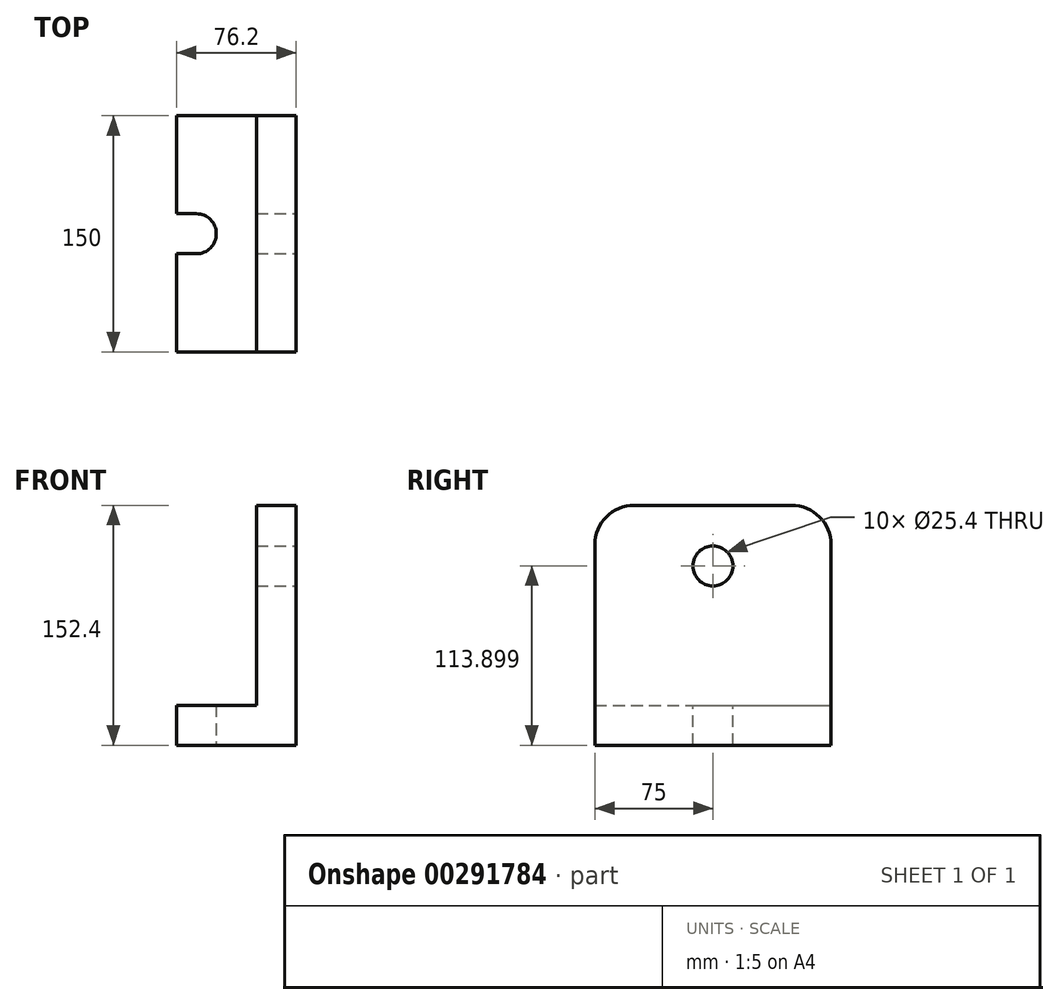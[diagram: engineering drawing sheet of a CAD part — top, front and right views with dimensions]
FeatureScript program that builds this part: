
annotation { "Feature Type Name" : "Feature", "Feature Type Description" : "" }
export const myFeature = defineFeature(function(context is Context, id is Id, definition is map)
    precondition{}
    {
        {
            var Q0;
            Q0=qCreatedBy(makeId("Front.planeOp"),FACE);
            var sketch = newSketch(context, id + "F0", { "sketchPlane" : qUnion([Q0])});
            skLineSegment(sketch, "E0.bottom", {"start": v(0, 0) * mm, "end": v(-76.2, 0) * mm});
            skLineSegment(sketch, "E0.top", {"start": v(-25.4, 25.4) * mm, "end": v(-76.2, 25.4) * mm});
            skLineSegment(sketch, "E0.right", {"start": v(-76.2, 0) * mm, "end": v(-76.2, 25.4) * mm});
            skLineSegment(sketch, "E1.top", {"start": v(0, 152.4) * mm, "end": v(-25.4, 152.4) * mm});
            skLineSegment(sketch, "E1.right", {"start": v(-25.4, 25.4) * mm, "end": v(-25.4, 152.4) * mm});
            skLineSegment(sketch, "E2", {"start": v(0, 152.4) * mm, "end": v(0, 0) * mm});
            skSolve(sketch);
        }
        {
            var Q0;
            Q0 = qSketchRegion(id + "F0", true);
            extrude(context, id + "F1", {"entities" : qUnion([Q0]), "endBound" : BoundingType.SYMMETRIC, "depth" : 150 * mm});
        }
        {
            var Q0;
            Q0=qCreatedBy(makeId("Right.planeOp"),FACE);
            var sketch = newSketch(context, id + "F2", { "sketchPlane" : qUnion([Q0])});
            skCircle(sketch, "E3", {"center": v(0, 113.9) * mm, "radius": 12.7 * mm});
            skSolve(sketch);
        }
        {
            var Q0;
            Q0=makeQuery(id+"F2.imprint","IMPRINT",FACE,{"disambiguationData":[TD([[makeQuery(id+"F2.imprint","IMPRINT",EDGE,{"derivedFrom":sQuery(id+"F2.wireOp",EDGE,"E3")}),1.0]])]});
            extrude(context, id + "F3", {"entities" : qUnion([Q0]), "operationType" : NewBodyOperationType.REMOVE, "oppositeDirection" : true, "depth" : 25.4 * mm});
        }
        {
            var Q0;
            Q0=qCreatedBy(makeId("Top.planeOp"),FACE);
            var sketch = newSketch(context, id + "F4", { "sketchPlane" : qUnion([Q0])});
            skLineSegment(sketch, "E4.bottom", {"start": v(-63.52, 12.7) * mm, "end": v(-76.22, 12.7) * mm});
            skLineSegment(sketch, "E4.top", {"start": v(-63.52, -12.7) * mm, "end": v(-76.22, -12.7) * mm});
            skLineSegment(sketch, "E4.right", {"start": v(-76.22, 12.7) * mm, "end": v(-76.22, -12.7) * mm});
            skPoint(sketch, "E4.middle", {"position": v(-69.87, 0) * mm});
            skArc(sketch, "E5", {"start": v(-63.52, -12.7) * mm, "mid": v(-50.82, 0) * mm, "end": v(-63.52, 12.7) * mm});
            skSolve(sketch);
        }
        {
            var Q0;
            Q0 = qSketchRegion(id + "F4", true);
            extrude(context, id + "F5", {"entities" : qUnion([Q0]), "operationType" : NewBodyOperationType.REMOVE, "depth" : 25.4 * mm});
        }
        {
            var Q0;
            Q0=makeQuery(id+"F1.opExtrude","CAP_EDGE",EDGE,{"disambiguationData":[OSD([sQuery(id+"F0.wireOp",EDGE,"E1.top")])],"isStart":false});
            fillet(context, id + "F6", {"entities" : qUnion([Q0]), "radius" : 25 * mm, "tangentPropagation" : true, "allowEdgeOverflow" : false});
        }
        {
            var Q0;
            Q0=makeQuery(id+"F1.opExtrude","CAP_EDGE",EDGE,{"disambiguationData":[OSD([sQuery(id+"F0.wireOp",EDGE,"E1.top")])],"isStart":true});
            fillet(context, id + "F7", {"entities" : qUnion([Q0]), "radius" : 25 * mm, "tangentPropagation" : true, "allowEdgeOverflow" : false});
        }
    });
